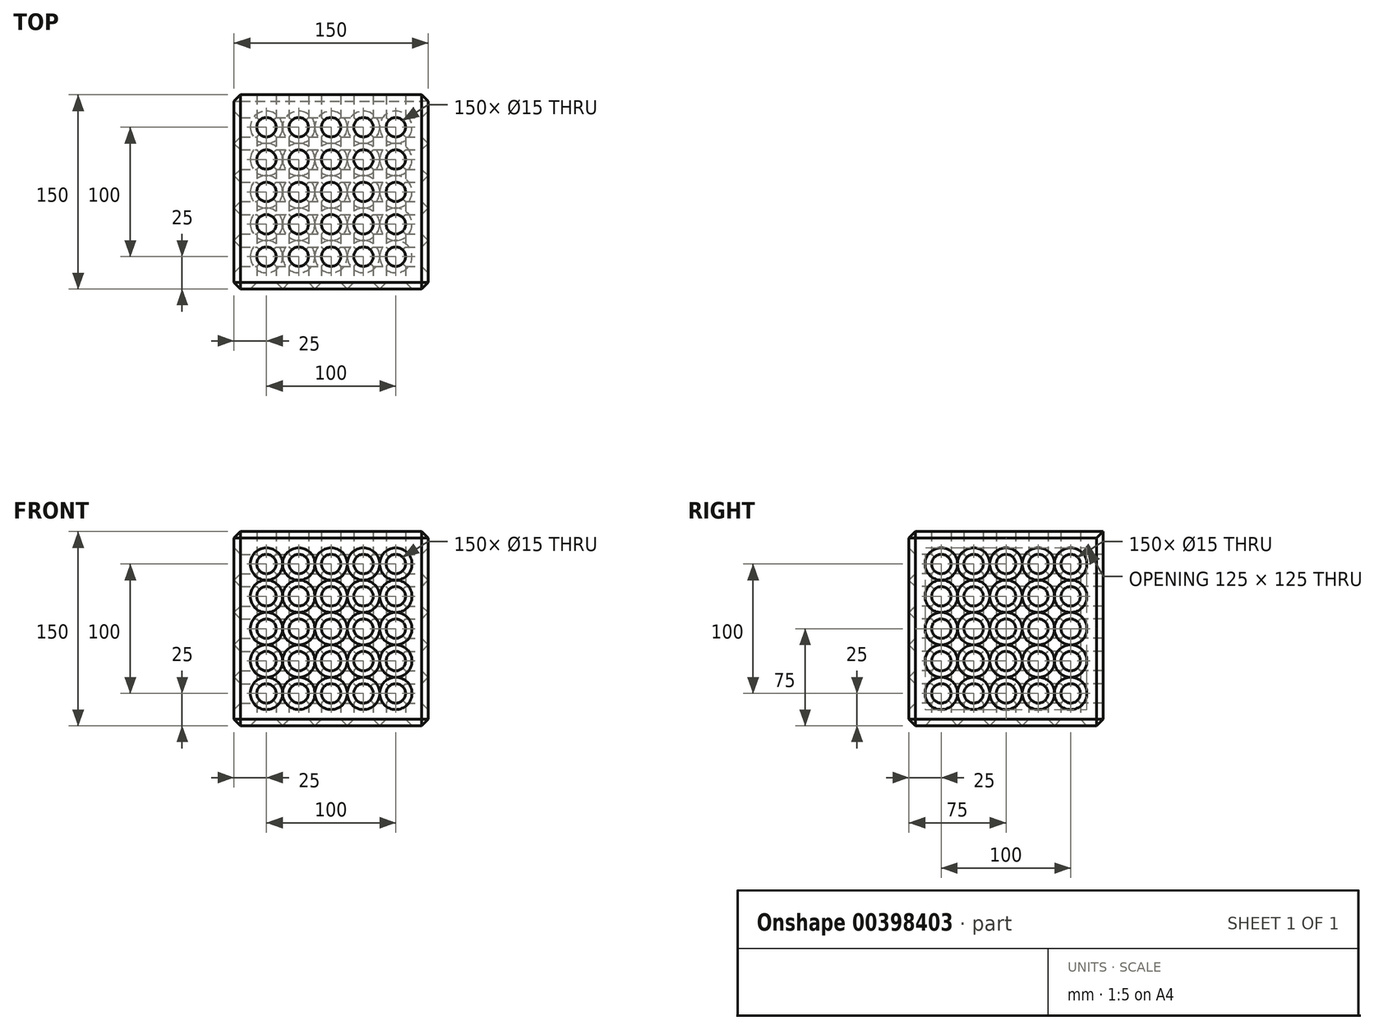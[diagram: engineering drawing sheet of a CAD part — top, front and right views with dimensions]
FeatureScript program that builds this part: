
annotation { "Feature Type Name" : "Feature", "Feature Type Description" : "" }
export const myFeature = defineFeature(function(context is Context, id is Id, definition is map)
    precondition{}
    {
        {
            var Q0;
            Q0=qCreatedBy(makeId("Front.planeOp"),FACE);
            var sketch = newSketch(context, id + "F0", { "sketchPlane" : qUnion([Q0])});
            skLineSegment(sketch, "E0.bottom", {"start": v(75, -75) * mm, "end": v(-75, -75) * mm});
            skLineSegment(sketch, "E0.top", {"start": v(75, 75) * mm, "end": v(-75, 75) * mm});
            skLineSegment(sketch, "E0.left", {"start": v(75, -75) * mm, "end": v(75, 75) * mm});
            skLineSegment(sketch, "E0.right", {"start": v(-75, -75) * mm, "end": v(-75, 75) * mm});
            skPoint(sketch, "E0.middle", {"position": v(0, 0) * mm});
            skSolve(sketch);
        }
        {
            var Q0;
            Q0=makeQuery(id+"F0.imprint","IMPRINT",FACE,{"disambiguationData":[TD([[makeQuery(id+"F0.imprint","IMPRINT",EDGE,{"derivedFrom":sQuery(id+"F0.wireOp",EDGE,"E0.bottom")}),-1.0]])]});
            extrude(context, id + "F1", {"entities" : qUnion([Q0]), "depth" : 150 * mm});
        }
        {
            var Q0;
            Q0=makeQuery(id+"F1.opExtrude","CAP_FACE",FACE,{"disambiguationData":[OSD([sQuery(id+"F0.wireOp",EDGE,"E0.bottom"),sQuery(id+"F0.wireOp",EDGE,"E0.top"),sQuery(id+"F0.wireOp",EDGE,"E0.left"),sQuery(id+"F0.wireOp",EDGE,"E0.right")])],"isStart":false});
            var sketch = newSketch(context, id + "F2", { "sketchPlane" : qUnion([Q0])});
            skCircle(sketch, "E1", {"center": v(50, 50) * mm, "radius": 7.5 * mm});
            skCircle(sketch, "E2.0.1.0", {"center": v(50, 25) * mm, "radius": 7.5 * mm});
            skCircle(sketch, "E2.0.2.0", {"center": v(50, 0) * mm, "radius": 7.5 * mm});
            skCircle(sketch, "E2.0.3.0", {"center": v(50, -25) * mm, "radius": 7.5 * mm});
            skCircle(sketch, "E2.0.4.0", {"center": v(50, -50) * mm, "radius": 7.5 * mm});
            skCircle(sketch, "E2.1.0.0", {"center": v(25, 50) * mm, "radius": 7.5 * mm});
            skCircle(sketch, "E2.1.1.0", {"center": v(25, 25) * mm, "radius": 7.5 * mm});
            skCircle(sketch, "E2.1.2.0", {"center": v(25, 0) * mm, "radius": 7.5 * mm});
            skCircle(sketch, "E2.1.3.0", {"center": v(25, -25) * mm, "radius": 7.5 * mm});
            skCircle(sketch, "E2.1.4.0", {"center": v(25, -50) * mm, "radius": 7.5 * mm});
            skCircle(sketch, "E2.2.0.0", {"center": v(0, 50) * mm, "radius": 7.5 * mm});
            skCircle(sketch, "E2.2.1.0", {"center": v(0, 25) * mm, "radius": 7.5 * mm});
            skCircle(sketch, "E2.2.2.0", {"center": v(0, 0) * mm, "radius": 7.5 * mm});
            skCircle(sketch, "E2.2.3.0", {"center": v(0, -25) * mm, "radius": 7.5 * mm});
            skCircle(sketch, "E2.2.4.0", {"center": v(0, -50) * mm, "radius": 7.5 * mm});
            skCircle(sketch, "E2.3.0.0", {"center": v(-25, 50) * mm, "radius": 7.5 * mm});
            skCircle(sketch, "E2.3.1.0", {"center": v(-25, 25) * mm, "radius": 7.5 * mm});
            skCircle(sketch, "E2.3.2.0", {"center": v(-25, 0) * mm, "radius": 7.5 * mm});
            skCircle(sketch, "E2.3.3.0", {"center": v(-25, -25) * mm, "radius": 7.5 * mm});
            skCircle(sketch, "E2.3.4.0", {"center": v(-25, -50) * mm, "radius": 7.5 * mm});
            skCircle(sketch, "E2.4.0.0", {"center": v(-50, 50) * mm, "radius": 7.5 * mm});
            skCircle(sketch, "E2.4.1.0", {"center": v(-50, 25) * mm, "radius": 7.5 * mm});
            skCircle(sketch, "E2.4.2.0", {"center": v(-50, 0) * mm, "radius": 7.5 * mm});
            skCircle(sketch, "E2.4.3.0", {"center": v(-50, -25) * mm, "radius": 7.5 * mm});
            skCircle(sketch, "E2.4.4.0", {"center": v(-50, -50) * mm, "radius": 7.5 * mm});
            skLineSegment(sketch, "E2.direction1", {"start": v(50, 50) * mm, "end": v(25, 50) * mm, "construction": true});
            skLineSegment(sketch, "E2.direction2", {"start": v(50, 50) * mm, "end": v(50, 25) * mm, "construction": true});
            skSolve(sketch);
        }
        {
            var Q0;
            Q0 = qSketchRegion(id + "F2", true);
            extrude(context, id + "F3", {"entities" : qUnion([Q0]), "operationType" : NewBodyOperationType.REMOVE, "endBound" : BoundingType.THROUGH_ALL, "oppositeDirection" : true, "depth" : 25 * mm});
        }
        {
            var Q0;
            Q0=makeQuery(id+"F1.opExtrude","SWEPT_FACE",FACE,{"disambiguationData":[OSD([sQuery(id+"F0.wireOp",EDGE,"E0.left")])]});
            var sketch = newSketch(context, id + "F4", { "sketchPlane" : qUnion([Q0])});
            skCircle(sketch, "E3", {"center": v(-25, 50) * mm, "radius": 7.5 * mm});
            skCircle(sketch, "E4.0.1.0", {"center": v(-25, 25) * mm, "radius": 7.5 * mm});
            skCircle(sketch, "E4.0.2.0", {"center": v(-25, 0) * mm, "radius": 7.5 * mm});
            skCircle(sketch, "E4.0.3.0", {"center": v(-25, -25) * mm, "radius": 7.5 * mm});
            skCircle(sketch, "E4.0.4.0", {"center": v(-25, -50) * mm, "radius": 7.5 * mm});
            skCircle(sketch, "E4.1.0.0", {"center": v(-50, 50) * mm, "radius": 7.5 * mm});
            skCircle(sketch, "E4.1.1.0", {"center": v(-50, 25) * mm, "radius": 7.5 * mm});
            skCircle(sketch, "E4.1.2.0", {"center": v(-50, 0) * mm, "radius": 7.5 * mm});
            skCircle(sketch, "E4.1.3.0", {"center": v(-50, -25) * mm, "radius": 7.5 * mm});
            skCircle(sketch, "E4.1.4.0", {"center": v(-50, -50) * mm, "radius": 7.5 * mm});
            skCircle(sketch, "E4.2.0.0", {"center": v(-75, 50) * mm, "radius": 7.5 * mm});
            skCircle(sketch, "E4.2.1.0", {"center": v(-75, 25) * mm, "radius": 7.5 * mm});
            skCircle(sketch, "E4.2.2.0", {"center": v(-75, 0) * mm, "radius": 7.5 * mm});
            skCircle(sketch, "E4.2.3.0", {"center": v(-75, -25) * mm, "radius": 7.5 * mm});
            skCircle(sketch, "E4.2.4.0", {"center": v(-75, -50) * mm, "radius": 7.5 * mm});
            skCircle(sketch, "E4.3.0.0", {"center": v(-100, 50) * mm, "radius": 7.5 * mm});
            skCircle(sketch, "E4.3.1.0", {"center": v(-100, 25) * mm, "radius": 7.5 * mm});
            skCircle(sketch, "E4.3.2.0", {"center": v(-100, 0) * mm, "radius": 7.5 * mm});
            skCircle(sketch, "E4.3.3.0", {"center": v(-100, -25) * mm, "radius": 7.5 * mm});
            skCircle(sketch, "E4.3.4.0", {"center": v(-100, -50) * mm, "radius": 7.5 * mm});
            skCircle(sketch, "E4.4.0.0", {"center": v(-125, 50) * mm, "radius": 7.5 * mm});
            skCircle(sketch, "E4.4.1.0", {"center": v(-125, 25) * mm, "radius": 7.5 * mm});
            skCircle(sketch, "E4.4.2.0", {"center": v(-125, 0) * mm, "radius": 7.5 * mm});
            skCircle(sketch, "E4.4.3.0", {"center": v(-125, -25) * mm, "radius": 7.5 * mm});
            skCircle(sketch, "E4.4.4.0", {"center": v(-125, -50) * mm, "radius": 7.5 * mm});
            skLineSegment(sketch, "E4.direction1", {"start": v(-25, 50) * mm, "end": v(-50, 50) * mm, "construction": true});
            skLineSegment(sketch, "E4.direction2", {"start": v(-25, 50) * mm, "end": v(-25, 25) * mm, "construction": true});
            skSolve(sketch);
        }
        {
            var Q0;
            Q0 = qSketchRegion(id + "F4", true);
            extrude(context, id + "F5", {"entities" : qUnion([Q0]), "operationType" : NewBodyOperationType.REMOVE, "endBound" : BoundingType.THROUGH_ALL, "oppositeDirection" : true, "depth" : 25 * mm});
        }
        {
            var Q0;
            Q0=makeQuery(id+"F1.opExtrude","SWEPT_FACE",FACE,{"disambiguationData":[OSD([sQuery(id+"F0.wireOp",EDGE,"E0.bottom")])]});
            var sketch = newSketch(context, id + "F6", { "sketchPlane" : qUnion([Q0])});
            skCircle(sketch, "E5", {"center": v(50, 125) * mm, "radius": 7.5 * mm});
            skCircle(sketch, "E6.0.1.0", {"center": v(50, 100) * mm, "radius": 7.5 * mm});
            skCircle(sketch, "E6.0.2.0", {"center": v(50, 75) * mm, "radius": 7.5 * mm});
            skCircle(sketch, "E6.0.3.0", {"center": v(50, 50) * mm, "radius": 7.5 * mm});
            skCircle(sketch, "E6.0.4.0", {"center": v(50, 25) * mm, "radius": 7.5 * mm});
            skCircle(sketch, "E6.1.0.0", {"center": v(25, 125) * mm, "radius": 7.5 * mm});
            skCircle(sketch, "E6.1.1.0", {"center": v(25, 100) * mm, "radius": 7.5 * mm});
            skCircle(sketch, "E6.1.2.0", {"center": v(25, 75) * mm, "radius": 7.5 * mm});
            skCircle(sketch, "E6.1.3.0", {"center": v(25, 50) * mm, "radius": 7.5 * mm});
            skCircle(sketch, "E6.1.4.0", {"center": v(25, 25) * mm, "radius": 7.5 * mm});
            skCircle(sketch, "E6.2.0.0", {"center": v(0, 125) * mm, "radius": 7.5 * mm});
            skCircle(sketch, "E6.2.1.0", {"center": v(0, 100) * mm, "radius": 7.5 * mm});
            skCircle(sketch, "E6.2.2.0", {"center": v(0, 75) * mm, "radius": 7.5 * mm});
            skCircle(sketch, "E6.2.3.0", {"center": v(0, 50) * mm, "radius": 7.5 * mm});
            skCircle(sketch, "E6.2.4.0", {"center": v(0, 25) * mm, "radius": 7.5 * mm});
            skCircle(sketch, "E6.3.0.0", {"center": v(-25, 125) * mm, "radius": 7.5 * mm});
            skCircle(sketch, "E6.3.1.0", {"center": v(-25, 100) * mm, "radius": 7.5 * mm});
            skCircle(sketch, "E6.3.2.0", {"center": v(-25, 75) * mm, "radius": 7.5 * mm});
            skCircle(sketch, "E6.3.3.0", {"center": v(-25, 50) * mm, "radius": 7.5 * mm});
            skCircle(sketch, "E6.3.4.0", {"center": v(-25, 25) * mm, "radius": 7.5 * mm});
            skCircle(sketch, "E6.4.0.0", {"center": v(-50, 125) * mm, "radius": 7.5 * mm});
            skCircle(sketch, "E6.4.1.0", {"center": v(-50, 100) * mm, "radius": 7.5 * mm});
            skCircle(sketch, "E6.4.2.0", {"center": v(-50, 75) * mm, "radius": 7.5 * mm});
            skCircle(sketch, "E6.4.3.0", {"center": v(-50, 50) * mm, "radius": 7.5 * mm});
            skCircle(sketch, "E6.4.4.0", {"center": v(-50, 25) * mm, "radius": 7.5 * mm});
            skLineSegment(sketch, "E6.direction1", {"start": v(50, 125) * mm, "end": v(25, 125) * mm, "construction": true});
            skLineSegment(sketch, "E6.direction2", {"start": v(50, 125) * mm, "end": v(50, 100) * mm, "construction": true});
            skSolve(sketch);
        }
        {
            var Q0;
            Q0 = qSketchRegion(id + "F6", true);
            extrude(context, id + "F7", {"entities" : qUnion([Q0]), "operationType" : NewBodyOperationType.REMOVE, "endBound" : BoundingType.THROUGH_ALL, "oppositeDirection" : true, "depth" : 25 * mm});
        }
        {
            var Q0;
            Q0=makeQuery(id+"F1.opExtrude","SWEPT_FACE",FACE,{"disambiguationData":[OSD([sQuery(id+"F0.wireOp",EDGE,"E0.right")])]});
            var Q1;
            Q1=makeQuery(id+"F1.opExtrude","SWEPT_FACE",FACE,{"disambiguationData":[OSD([sQuery(id+"F0.wireOp",EDGE,"E0.bottom")])]});
            var Q2;
            Q2=makeQuery(id+"F1.opExtrude","SWEPT_FACE",FACE,{"disambiguationData":[OSD([sQuery(id+"F0.wireOp",EDGE,"E0.left")])]});
            var Q3;
            Q3=makeQuery(id+"F1.opExtrude","CAP_FACE",FACE,{"disambiguationData":[OSD([sQuery(id+"F0.wireOp",EDGE,"E0.bottom"),sQuery(id+"F0.wireOp",EDGE,"E0.top"),sQuery(id+"F0.wireOp",EDGE,"E0.left"),sQuery(id+"F0.wireOp",EDGE,"E0.right")])],"isStart":false});
            chamfer(context, id + "F8", {"entities" : qUnion([Q0, Q1, Q2, Q3]), "width" : 5 * mm, "tangentPropagation" : true});
        }
    });
